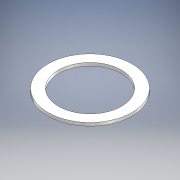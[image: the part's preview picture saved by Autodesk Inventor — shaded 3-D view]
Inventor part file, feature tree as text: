
AUTODESK INVENTOR PART (.ipt)
format: ipt  version: 2016 (Build 200138000, 138)  size: 97,280 bytes
history: native  units: mm
features: other x1, extrude x1, sketch x1
ambient origin geometry x8: Origin, YZ Plane, XZ Plane, XY Plane, X Axis, Y Axis, Z Axis, Center Point
bodies: Body1 (feature_tree)
feature tree (3):
  other  "ソリッド1"
  extrude  "押し出し1"  Depth=6.0mm
  sketch  "スケッチ1"
